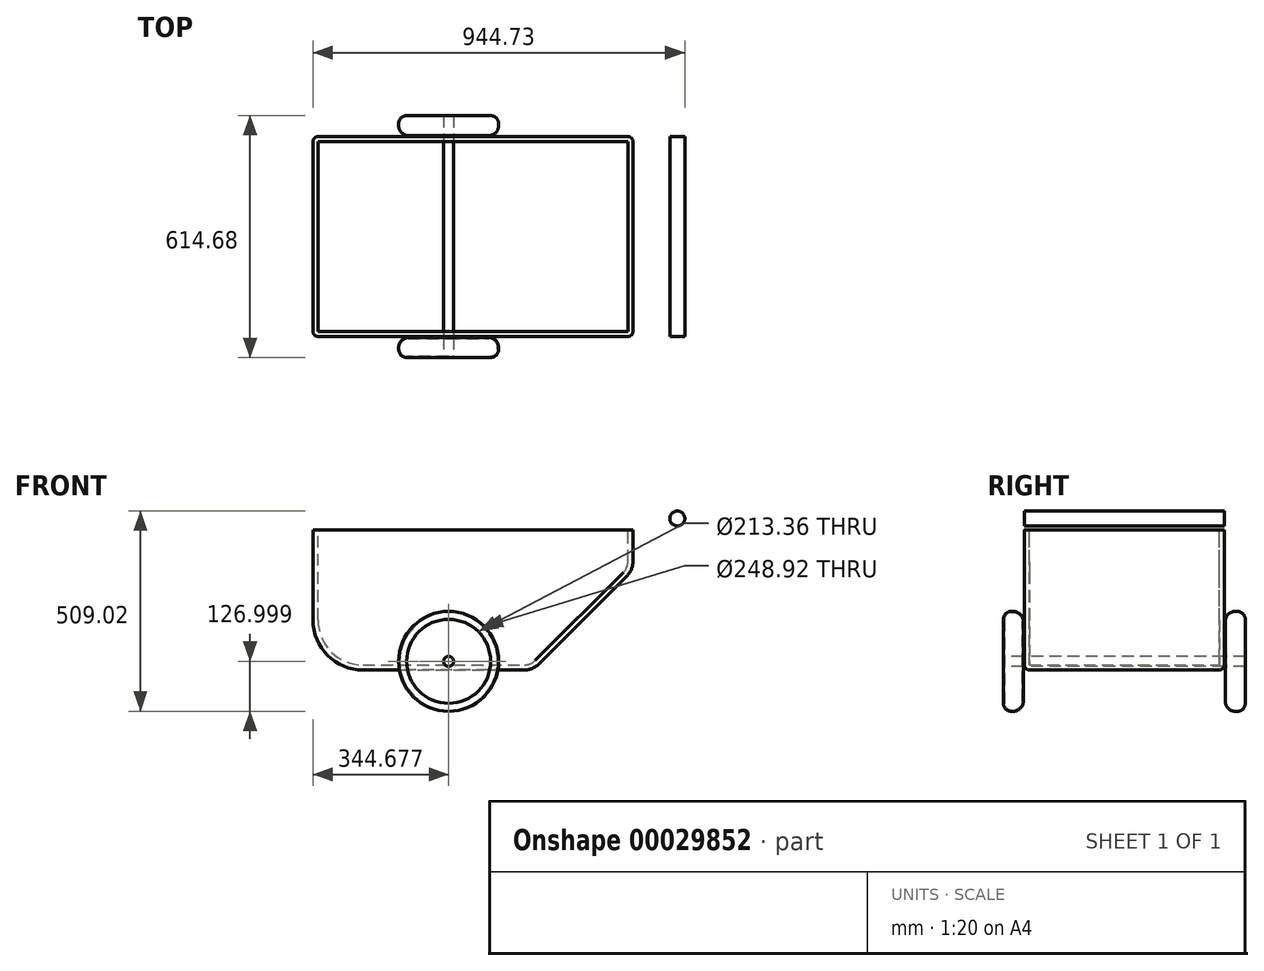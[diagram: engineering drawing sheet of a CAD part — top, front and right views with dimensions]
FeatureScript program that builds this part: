
annotation { "Feature Type Name" : "Feature", "Feature Type Description" : "" }
export const myFeature = defineFeature(function(context is Context, id is Id, definition is map)
    precondition{}
    {
        {
            var Q0;
            Q0=qCreatedBy(makeId("Top.planeOp"),FACE);
            var sketch = newSketch(context, id + "F0", { "sketchPlane" : qUnion([Q0])});
            skLineSegment(sketch, "E0", {"start": v(0, 0) * mm, "end": v(812.8, 0) * mm});
            skLineSegment(sketch, "E1", {"start": v(812.8, 0) * mm, "end": v(812.8, 508) * mm});
            skLineSegment(sketch, "E2", {"start": v(812.8, 508) * mm, "end": v(0, 508) * mm});
            skLineSegment(sketch, "E3", {"start": v(0, 508) * mm, "end": v(0, 0) * mm});
            skSolve(sketch);
        }
        {
            var Q0;
            Q0=makeQuery(id+"F0.imprint","IMPRINT",FACE,{"disambiguationData":[TD([[makeQuery(id+"F0.imprint","IMPRINT",EDGE,{"derivedFrom":sQuery(id+"F0.wireOp",EDGE,"E0")}),1.0]])]});
            extrude(context, id + "F1", {"entities" : qUnion([Q0]), "depth" : 355.6 * mm});
        }
        {
            var Q0;
            Q0=makeQuery(id+"F1.opExtrude","CAP_EDGE",EDGE,{"disambiguationData":[OSD([sQuery(id+"F0.wireOp",EDGE,"E1")])],"isStart":true});
            chamfer(context, id + "F2", {"entities" : qUnion([Q0]), "width" : 254 * mm, "tangentPropagation" : true});
        }
        {
            var Q0;
            Q0=makeQuery(id+"F1.opExtrude","CAP_EDGE",EDGE,{"disambiguationData":[OSD([sQuery(id+"F0.wireOp",EDGE,"E3")])],"isStart":true});
            fillet(context, id + "F3", {"entities" : qUnion([Q0]), "radius" : 127 * mm, "tangentPropagation" : true, "allowEdgeOverflow" : false});
        }
        {
            var Q0;
            {var subQ0=sQuery(id+"F0.wireOp",EDGE,"E1");Q0=makeQuery(id+"F2.opChamfer","BLEND_EDGE",EDGE,{"blendedFrom":[makeQuery(id+"F1.opExtrude","CAP_EDGE",EDGE,{"disambiguationData":[OSD([subQ0])],"isStart":true}),makeQuery(id+"F1.opExtrude","CAP_FACE",FACE,{"disambiguationData":[OSD([sQuery(id+"F0.wireOp",EDGE,"E0"),subQ0,sQuery(id+"F0.wireOp",EDGE,"E2"),sQuery(id+"F0.wireOp",EDGE,"E3")])],"isStart":true})],"blendedInto":[makeQuery(id+"F1.opExtrude","CAP_FACE",FACE,{"disambiguationData":[OSD([sQuery(id+"F0.wireOp",EDGE,"E0"),subQ0,sQuery(id+"F0.wireOp",EDGE,"E2"),sQuery(id+"F0.wireOp",EDGE,"E3")])],"isStart":true})]});}
            fillet(context, id + "F4", {"entities" : qUnion([Q0]), "radius" : 50.8 * mm, "tangentPropagation" : true, "allowEdgeOverflow" : false});
        }
        {
            var Q0;
            {var subQ0=sQuery(id+"F0.wireOp",EDGE,"E1");Q0=makeQuery(id+"F2.opChamfer","BLEND_EDGE",EDGE,{"blendedFrom":[makeQuery(id+"F1.opExtrude","CAP_EDGE",EDGE,{"disambiguationData":[OSD([subQ0])],"isStart":true}),makeQuery(id+"F1.opExtrude","SWEPT_FACE",FACE,{"disambiguationData":[OSD([subQ0])]})],"blendedInto":[makeQuery(id+"F1.opExtrude","SWEPT_FACE",FACE,{"disambiguationData":[OSD([subQ0])]})]});}
            fillet(context, id + "F5", {"entities" : qUnion([Q0]), "radius" : 50.8 * mm, "tangentPropagation" : true, "allowEdgeOverflow" : false});
        }
        {
            var Q0;
            Q0=makeQuery(id+"F1.opExtrude","CAP_EDGE",EDGE,{"disambiguationData":[OSD([sQuery(id+"F0.wireOp",EDGE,"E0")])],"isStart":true});
            var Q1;
            {var subQ0=sQuery(id+"F0.wireOp",EDGE,"E1");var subQ1=sQuery(id+"F0.wireOp",EDGE,"E0");Q1=makeQuery(id+"F4.opFillet","BLEND_EDGE",EDGE,{"blendedFrom":[makeQuery(id+"F2.opChamfer","BLEND_EDGE",EDGE,{"blendedFrom":[makeQuery(id+"F1.opExtrude","CAP_EDGE",EDGE,{"disambiguationData":[OSD([subQ0])],"isStart":true}),makeQuery(id+"F1.opExtrude","CAP_FACE",FACE,{"disambiguationData":[OSD([subQ1,subQ0,sQuery(id+"F0.wireOp",EDGE,"E2"),sQuery(id+"F0.wireOp",EDGE,"E3")])],"isStart":true})],"blendedInto":[makeQuery(id+"F1.opExtrude","CAP_FACE",FACE,{"disambiguationData":[OSD([subQ1,subQ0,sQuery(id+"F0.wireOp",EDGE,"E2"),sQuery(id+"F0.wireOp",EDGE,"E3")])],"isStart":true})]}),makeQuery(id+"F1.opExtrude","SWEPT_FACE",FACE,{"disambiguationData":[OSD([subQ1])]})],"blendedInto":[makeQuery(id+"F1.opExtrude","SWEPT_FACE",FACE,{"disambiguationData":[OSD([subQ1])]})]});}
            var Q2;
            Q2=makeQuery(id+"F2.opChamfer","BLEND_EDGE",EDGE,{"blendedFrom":[makeQuery(id+"F1.opExtrude","CAP_EDGE",EDGE,{"disambiguationData":[OSD([sQuery(id+"F0.wireOp",EDGE,"E1")])],"isStart":true}),makeQuery(id+"F1.opExtrude","SWEPT_FACE",FACE,{"disambiguationData":[OSD([sQuery(id+"F0.wireOp",EDGE,"E0")])]})],"blendedInto":[makeQuery(id+"F1.opExtrude","SWEPT_FACE",FACE,{"disambiguationData":[OSD([sQuery(id+"F0.wireOp",EDGE,"E0")])]})]});
            var Q3;
            {var subQ0=sQuery(id+"F0.wireOp",EDGE,"E1");Q3=makeQuery(id+"F5.opFillet","BLEND_EDGE",EDGE,{"blendedFrom":[makeQuery(id+"F2.opChamfer","BLEND_EDGE",EDGE,{"blendedFrom":[makeQuery(id+"F1.opExtrude","CAP_EDGE",EDGE,{"disambiguationData":[OSD([subQ0])],"isStart":true}),makeQuery(id+"F1.opExtrude","SWEPT_FACE",FACE,{"disambiguationData":[OSD([subQ0])]})],"blendedInto":[makeQuery(id+"F1.opExtrude","SWEPT_FACE",FACE,{"disambiguationData":[OSD([subQ0])]})]}),makeQuery(id+"F1.opExtrude","SWEPT_FACE",FACE,{"disambiguationData":[OSD([sQuery(id+"F0.wireOp",EDGE,"E0")])]})],"blendedInto":[makeQuery(id+"F1.opExtrude","SWEPT_FACE",FACE,{"disambiguationData":[OSD([sQuery(id+"F0.wireOp",EDGE,"E0")])]})]});}
            var Q4;
            Q4=makeQuery(id+"F1.opExtrude","SWEPT_EDGE",EDGE,{"disambiguationData":[OSD([sQuery(id+"F0.wireOp",EDGE,"E0"),sQuery(id+"F0.wireOp",EDGE,"E1")])]});
            var Q5;
            Q5=makeQuery(id+"F3.opFillet","BLEND_EDGE",EDGE,{"blendedFrom":[makeQuery(id+"F1.opExtrude","CAP_EDGE",EDGE,{"disambiguationData":[OSD([sQuery(id+"F0.wireOp",EDGE,"E3")])],"isStart":true}),makeQuery(id+"F1.opExtrude","SWEPT_FACE",FACE,{"disambiguationData":[OSD([sQuery(id+"F0.wireOp",EDGE,"E0")])]})],"blendedInto":[makeQuery(id+"F1.opExtrude","SWEPT_FACE",FACE,{"disambiguationData":[OSD([sQuery(id+"F0.wireOp",EDGE,"E0")])]})]});
            var Q6;
            Q6=makeQuery(id+"F1.opExtrude","SWEPT_EDGE",EDGE,{"disambiguationData":[OSD([sQuery(id+"F0.wireOp",EDGE,"E0"),sQuery(id+"F0.wireOp",EDGE,"E3")])]});
            fillet(context, id + "F6", {"entities" : qUnion([Q0, Q1, Q2, Q3, Q4, Q5, Q6]), "radius" : 12.7 * mm, "tangentPropagation" : true, "allowEdgeOverflow" : false});
        }
        {
            var Q0;
            Q0=makeQuery(id+"F1.opExtrude","SWEPT_EDGE",EDGE,{"disambiguationData":[OSD([sQuery(id+"F0.wireOp",EDGE,"E2"),sQuery(id+"F0.wireOp",EDGE,"E3")])]});
            var Q1;
            Q1=makeQuery(id+"F3.opFillet","BLEND_EDGE",EDGE,{"blendedFrom":[makeQuery(id+"F1.opExtrude","CAP_EDGE",EDGE,{"disambiguationData":[OSD([sQuery(id+"F0.wireOp",EDGE,"E3")])],"isStart":true}),makeQuery(id+"F1.opExtrude","SWEPT_FACE",FACE,{"disambiguationData":[OSD([sQuery(id+"F0.wireOp",EDGE,"E2")])]})],"blendedInto":[makeQuery(id+"F1.opExtrude","SWEPT_FACE",FACE,{"disambiguationData":[OSD([sQuery(id+"F0.wireOp",EDGE,"E2")])]})]});
            var Q2;
            Q2=makeQuery(id+"F1.opExtrude","CAP_EDGE",EDGE,{"disambiguationData":[OSD([sQuery(id+"F0.wireOp",EDGE,"E2")])],"isStart":true});
            var Q3;
            {var subQ0=sQuery(id+"F0.wireOp",EDGE,"E1");var subQ1=sQuery(id+"F0.wireOp",EDGE,"E2");Q3=makeQuery(id+"F4.opFillet","BLEND_EDGE",EDGE,{"blendedFrom":[makeQuery(id+"F2.opChamfer","BLEND_EDGE",EDGE,{"blendedFrom":[makeQuery(id+"F1.opExtrude","CAP_EDGE",EDGE,{"disambiguationData":[OSD([subQ0])],"isStart":true}),makeQuery(id+"F1.opExtrude","CAP_FACE",FACE,{"disambiguationData":[OSD([sQuery(id+"F0.wireOp",EDGE,"E0"),subQ0,subQ1,sQuery(id+"F0.wireOp",EDGE,"E3")])],"isStart":true})],"blendedInto":[makeQuery(id+"F1.opExtrude","CAP_FACE",FACE,{"disambiguationData":[OSD([sQuery(id+"F0.wireOp",EDGE,"E0"),subQ0,subQ1,sQuery(id+"F0.wireOp",EDGE,"E3")])],"isStart":true})]}),makeQuery(id+"F1.opExtrude","SWEPT_FACE",FACE,{"disambiguationData":[OSD([subQ1])]})],"blendedInto":[makeQuery(id+"F1.opExtrude","SWEPT_FACE",FACE,{"disambiguationData":[OSD([subQ1])]})]});}
            var Q4;
            Q4=makeQuery(id+"F2.opChamfer","BLEND_EDGE",EDGE,{"blendedFrom":[makeQuery(id+"F1.opExtrude","CAP_EDGE",EDGE,{"disambiguationData":[OSD([sQuery(id+"F0.wireOp",EDGE,"E1")])],"isStart":true}),makeQuery(id+"F1.opExtrude","SWEPT_FACE",FACE,{"disambiguationData":[OSD([sQuery(id+"F0.wireOp",EDGE,"E2")])]})],"blendedInto":[makeQuery(id+"F1.opExtrude","SWEPT_FACE",FACE,{"disambiguationData":[OSD([sQuery(id+"F0.wireOp",EDGE,"E2")])]})]});
            var Q5;
            {var subQ0=sQuery(id+"F0.wireOp",EDGE,"E1");Q5=makeQuery(id+"F5.opFillet","BLEND_EDGE",EDGE,{"blendedFrom":[makeQuery(id+"F2.opChamfer","BLEND_EDGE",EDGE,{"blendedFrom":[makeQuery(id+"F1.opExtrude","CAP_EDGE",EDGE,{"disambiguationData":[OSD([subQ0])],"isStart":true}),makeQuery(id+"F1.opExtrude","SWEPT_FACE",FACE,{"disambiguationData":[OSD([subQ0])]})],"blendedInto":[makeQuery(id+"F1.opExtrude","SWEPT_FACE",FACE,{"disambiguationData":[OSD([subQ0])]})]}),makeQuery(id+"F1.opExtrude","SWEPT_FACE",FACE,{"disambiguationData":[OSD([sQuery(id+"F0.wireOp",EDGE,"E2")])]})],"blendedInto":[makeQuery(id+"F1.opExtrude","SWEPT_FACE",FACE,{"disambiguationData":[OSD([sQuery(id+"F0.wireOp",EDGE,"E2")])]})]});}
            var Q6;
            Q6=makeQuery(id+"F1.opExtrude","SWEPT_EDGE",EDGE,{"disambiguationData":[OSD([sQuery(id+"F0.wireOp",EDGE,"E1"),sQuery(id+"F0.wireOp",EDGE,"E2")])]});
            fillet(context, id + "F7", {"entities" : qUnion([Q0, Q1, Q2, Q3, Q4, Q5, Q6]), "radius" : 12.7 * mm, "tangentPropagation" : true, "allowEdgeOverflow" : false});
        }
        {
            var Q0;
            Q0=makeQuery(id+"F1.opExtrude","CAP_FACE",FACE,{"disambiguationData":[OSD([sQuery(id+"F0.wireOp",EDGE,"E0"),sQuery(id+"F0.wireOp",EDGE,"E1"),sQuery(id+"F0.wireOp",EDGE,"E2"),sQuery(id+"F0.wireOp",EDGE,"E3")])],"isStart":false});
            shell(context, id + "F8", {"entities" : qUnion([Q0]), "thickness" : 12.7 * mm});
        }
        {
            var Q0;
            Q0=makeQuery(id+"F1.opExtrude","SWEPT_FACE",FACE,{"disambiguationData":[OSD([sQuery(id+"F0.wireOp",EDGE,"E2")])]});
            var sketch = newSketch(context, id + "F9", { "sketchPlane" : qUnion([Q0])});
            skLineSegment(sketch, "E4", {"start": v(-564.7, 23.86) * mm, "end": v(-925.68, 384.84) * mm});
            skCircle(sketch, "E5", {"center": v(-925.68, 384.84) * mm, "radius": 19.04 * mm});
            skSolve(sketch);
        }
        {
            var Q0;
            Q0=makeQuery(id+"F1.opExtrude","SWEPT_FACE",FACE,{"disambiguationData":[OSD([sQuery(id+"F0.wireOp",EDGE,"E0")])]});
            cPlane(context, id + "F10", {"entities" : qUnion([Q0]), "cplaneType" : CPlaneType.OFFSET, "offset" : 2.54 * mm, "width" : 152.4 * mm, "height" : 152.4 * mm});
        }
        {
            var Q0;
            Q0=qCreatedBy(id+"F10.planeOp",FACE);
            var sketch = newSketch(context, id + "F11", { "sketchPlane" : qUnion([Q0])});
            skCircle(sketch, "E6", {"center": v(344.68, 21.87) * mm, "radius": 127 * mm});
            skSolve(sketch);
        }
        {
            var Q0;
            Q0=makeQuery(id+"F11.imprint","IMPRINT",FACE,{"disambiguationData":[TD([[makeQuery(id+"F11.imprint","IMPRINT",EDGE,{"derivedFrom":sQuery(id+"F11.wireOp",EDGE,"E6")}),1.0]])]});
            extrude(context, id + "F12", {"entities" : qUnion([Q0]), "depth" : 50.8 * mm});
        }
        {
            var Q0;
            Q0=makeQuery(id+"F12.opExtrude","CAP_EDGE",EDGE,{"disambiguationData":[OSD([sQuery(id+"F11.wireOp",EDGE,"E6")])],"isStart":false});
            fillet(context, id + "F13", {"entities" : qUnion([Q0]), "radius" : 20.32 * mm, "tangentPropagation" : true, "allowEdgeOverflow" : false});
        }
        {
            var Q0;
            Q0=makeQuery(id+"F12.opExtrude","CAP_EDGE",EDGE,{"disambiguationData":[OSD([sQuery(id+"F11.wireOp",EDGE,"E6")])],"isStart":true});
            fillet(context, id + "F14", {"entities" : qUnion([Q0]), "radius" : 25.4 * mm, "tangentPropagation" : true, "allowEdgeOverflow" : false});
        }
        {
            var Q0;
            Q0=makeQuery(id+"F12.opExtrude","CAP_FACE",FACE,{"disambiguationData":[OSD([sQuery(id+"F11.wireOp",EDGE,"E6")])],"isStart":false});
            var sketch = newSketch(context, id + "F15", { "sketchPlane" : qUnion([Q0])});
            skCircle(sketch, "E7", {"center": v(344.68, 21.87) * mm, "radius": 12.7 * mm});
            skSolve(sketch);
        }
        {
            var Q0;
            Q0=makeQuery(id+"F1.opExtrude","SWEPT_FACE",FACE,{"disambiguationData":[OSD([sQuery(id+"F0.wireOp",EDGE,"E0")])]});
            cPlane(context, id + "F16", {"entities" : qUnion([Q0]), "cplaneType" : CPlaneType.OFFSET, "offset" : 254 * mm, "oppositeDirection" : true, "width" : 152.4 * mm, "height" : 152.4 * mm});
        }
        {
            var Q0;
            Q0=makeQuery(id+"F12.opExtrude","SWEPT_BODY",BODY,{"disambiguationData":[OSD([sQuery(id+"F11.wireOp",EDGE,"E6")])]});
            var Q1;
            Q1=qCreatedBy(id+"F16.planeOp",FACE);
            mirror(context, id + "F17", {"entities" : qUnion([Q0]), "mirrorPlane" : qUnion([Q1])});
        }
        {
            var Q0;
            Q0=makeQuery(id+"F15.imprint","IMPRINT",FACE,{"disambiguationData":[TD([[makeQuery(id+"F15.imprint","IMPRINT",EDGE,{"derivedFrom":sQuery(id+"F15.wireOp",EDGE,"E7")}),1.0]])]});
            var Q1;
            Q1=makeQuery(id+"F17.opPattern","COPY",FACE,{"derivedFrom":makeQuery(id+"F12.opExtrude","CAP_FACE",FACE,{"disambiguationData":[OSD([sQuery(id+"F11.wireOp",EDGE,"E6")])],"isStart":false}),"instanceName":"1"});
            extrude(context, id + "F18", {"entities" : qUnion([Q0]), "endBound" : BoundingType.UP_TO_SURFACE, "oppositeDirection" : true, "endBoundEntityFace" : qUnion([Q1]), "depth" : 25.4 * mm});
        }
        {
            var Q0;
            Q0=makeQuery(id+"F12.opExtrude","CAP_FACE",FACE,{"disambiguationData":[OSD([sQuery(id+"F11.wireOp",EDGE,"E6")])],"isStart":false});
            shell(context, id + "F19", {"entities" : qUnion([Q0]), "thickness" : 2.54 * mm});
        }
        {
            var Q0;
            Q0=makeQuery(id+"F9.imprint","IMPRINT",FACE,{"disambiguationData":[TD([[makeQuery(id+"F9.imprint","IMPRINT",EDGE,{"derivedFrom":sQuery(id+"F9.wireOp",EDGE,"E5")}),1.0]])]});
            var Q1;
            Q1=makeQuery(id+"F1.opExtrude","SWEPT_FACE",FACE,{"disambiguationData":[OSD([sQuery(id+"F0.wireOp",EDGE,"E0")])]});
            extrude(context, id + "F20", {"entities" : qUnion([Q0]), "endBound" : BoundingType.UP_TO_SURFACE, "oppositeDirection" : true, "endBoundEntityFace" : qUnion([Q1]), "depth" : 25.4 * mm});
        }
    });
